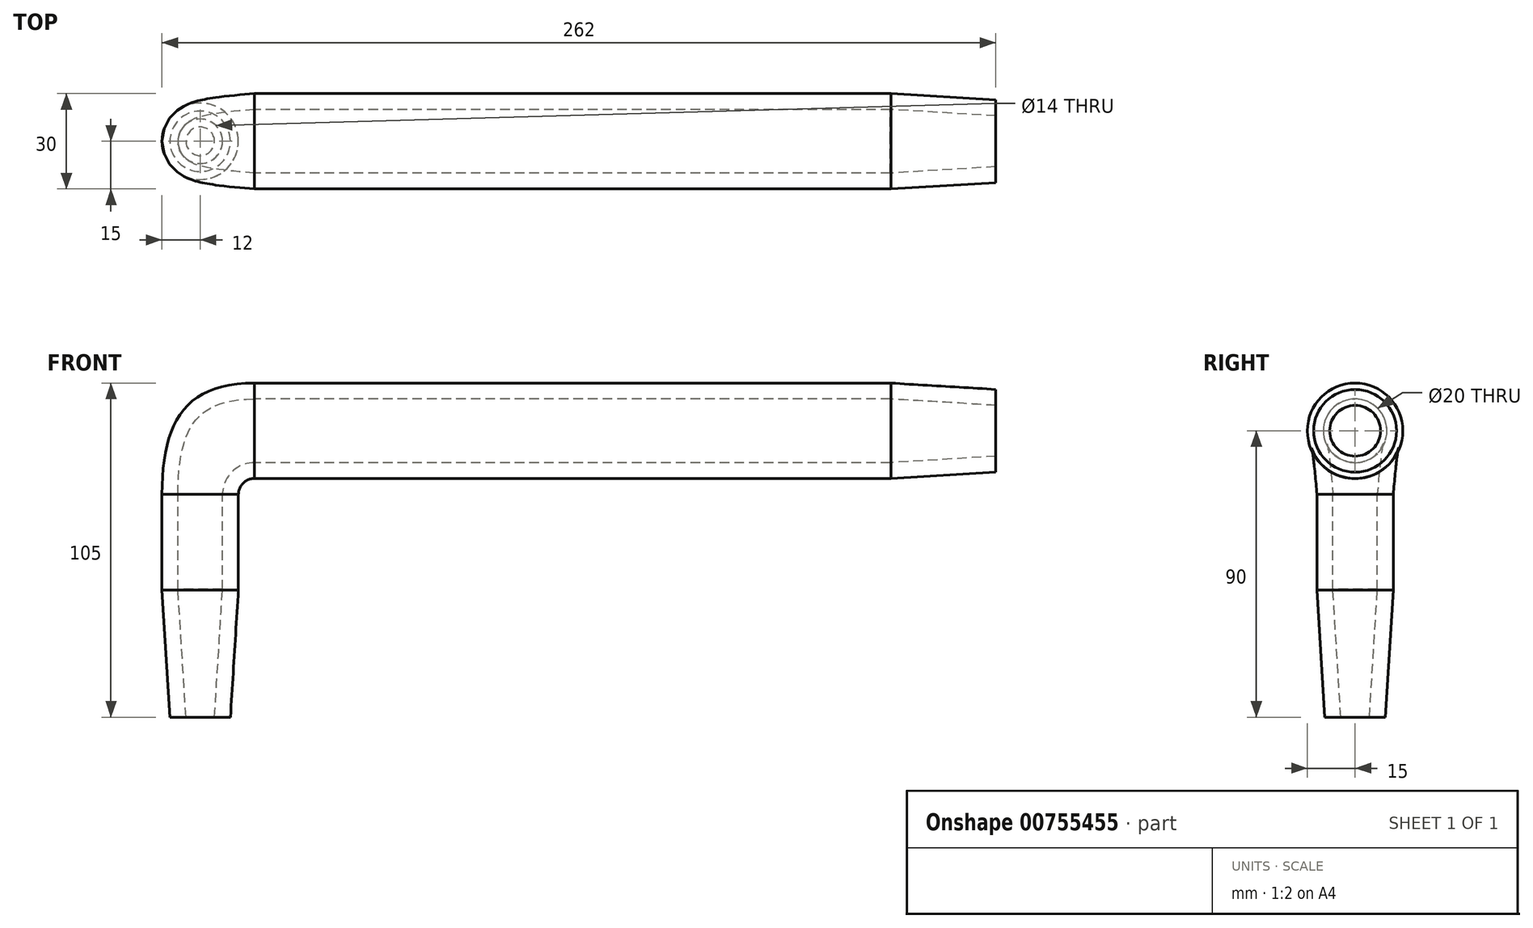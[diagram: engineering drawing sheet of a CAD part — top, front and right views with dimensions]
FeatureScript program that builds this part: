
annotation { "Feature Type Name" : "Feature", "Feature Type Description" : "" }
export const myFeature = defineFeature(function(context is Context, id is Id, definition is map)
    precondition{}
    {
        {
            var Q0;
            Q0=qCreatedBy(makeId("Front.planeOp"),FACE);
            var sketch = newSketch(context, id + "F0", { "sketchPlane" : qUnion([Q0])});
            skLineSegment(sketch, "E0", {"start": v(0, 0) * mm, "end": v(-29, 0) * mm, "construction": true});
            skLineSegment(sketch, "E1", {"start": v(0, 0) * mm, "end": v(0, 35) * mm, "construction": true});
            skArc(sketch, "E2", {"start": v(0, 5) * mm, "mid": v(-3.54, 3.54) * mm, "end": v(-5, 0) * mm});
            skFitSpline(sketch, "E3", {"points": [v(0, 35) * mm, v(-29, 0) * mm], "startDerivative": vector(-66.6, 0) * mm, "endDerivative": vector(0, -66.6) * mm});
            skLineSegment(sketch, "E4", {"start": v(0, 35) * mm, "end": v(18.57, 35) * mm, "construction": true});
            skLineSegment(sketch, "E5", {"start": v(-29, 0) * mm, "end": v(-29, -20.06) * mm, "construction": true});
            skSolve(sketch);
        }
        {
            var Q0;
            Q0=qCreatedBy(makeId("Top.planeOp"),FACE);
            var sketch = newSketch(context, id + "F1", { "sketchPlane" : qUnion([Q0])});
            skCircle(sketch, "E6", {"center": v(-17, 0) * mm, "radius": 12 * mm});
            skSolve(sketch);
        }
        {
            var Q0;
            Q0=qCreatedBy(makeId("Right.planeOp"),FACE);
            var sketch = newSketch(context, id + "F2", { "sketchPlane" : qUnion([Q0])});
            skCircle(sketch, "E7", {"center": v(0, 20) * mm, "radius": 15 * mm});
            skSolve(sketch);
        }
        {
            var Q0;
            Q0=makeQuery(id+"F1.imprint","IMPRINT",FACE,{"disambiguationData":[TD([[makeQuery(id+"F1.imprint","IMPRINT",EDGE,{"derivedFrom":sQuery(id+"F1.wireOp",EDGE,"E6")}),1.0]])]});
            var Q1;
            Q1=makeQuery(id+"F2.imprint","IMPRINT",FACE,{"disambiguationData":[TD([[makeQuery(id+"F2.imprint","IMPRINT",EDGE,{"derivedFrom":sQuery(id+"F2.wireOp",EDGE,"E7")}),1.0]])]});
            var Q2;
            Q2=sQuery(id+"F0.wireOp",EDGE,"E3");
            var Q3;
            Q3=sQuery(id+"F0.wireOp",EDGE,"E2");
            loft(context, id + "F3", {"addGuides" : true, "sheetProfilesArray" : [{ "sheetProfileEntities" : qUnion([Q0]) }, { "sheetProfileEntities" : qUnion([Q1]) }], "guidesArray" : [{ "guideEntities" : qUnion([Q2]), "guideDerivativeType" : LoftGuideDerivativeType.DEFAULT, "guideDerivativeMagnitude" : 1 }, { "guideEntities" : qUnion([Q3]), "guideDerivativeType" : LoftGuideDerivativeType.DEFAULT, "guideDerivativeMagnitude" : 1 }]});
        }
        {
            var Q0;
            Q0 = qSketchRegion(id + "F1", true);
            extrude(context, id + "F4", {"entities" : qUnion([Q0]), "operationType" : NewBodyOperationType.ADD, "oppositeDirection" : true, "depth" : 30 * mm, "offsetDistance" : 25 * mm});
        }
        {
            var Q0;
            Q0 = qSketchRegion(id + "F2", true);
            var Q1;
            Q1 = qSketchRegion(id + "F0", true);
            extrude(context, id + "F5", {"entities" : qUnion([Q0, Q1]), "operationType" : NewBodyOperationType.ADD, "depth" : 200 * mm, "offsetDistance" : 25 * mm});
        }
        {
            var Q0;
            Q0=qCreatedBy(makeId("Front.planeOp"),FACE);
            var sketch = newSketch(context, id + "F6", { "sketchPlane" : qUnion([Q0])});
            skLineSegment(sketch, "E8", {"start": v(-17, -30) * mm, "end": v(-17, -70) * mm});
            skLineSegment(sketch, "E9", {"start": v(-17, -70) * mm, "end": v(-7.5, -70) * mm});
            skLineSegment(sketch, "E10", {"start": v(-7.5, -70) * mm, "end": v(-5, -30) * mm});
            skLineSegment(sketch, "E11", {"start": v(-5, -30) * mm, "end": v(-17, -30) * mm});
            skLineSegment(sketch, "E12", {"start": v(-17, -30) * mm, "end": v(-29, -30) * mm, "construction": true});
            skSolve(sketch);
        }
        {
            var Q0;
            Q0 = qSketchRegion(id + "F6", true);
            var Q1;
            Q1=sQuery(id+"F6.wireOp",EDGE,"E8");
            revolve(context, id + "F7", {"operationType" : NewBodyOperationType.ADD, "surfaceOperationType" : NewSurfaceOperationType.NEW, "entities" : qUnion([Q0]), "axis" : qUnion([Q1]), "revolveType" : RevolveType.FULL});
        }
        {
            var Q0;
            Q0=qCreatedBy(makeId("Front.planeOp"),FACE);
            var sketch = newSketch(context, id + "F8", { "sketchPlane" : qUnion([Q0])});
            skLineSegment(sketch, "E13", {"start": v(200, 35) * mm, "end": v(200, 20) * mm});
            skLineSegment(sketch, "E14", {"start": v(200, 20) * mm, "end": v(233, 20) * mm});
            skLineSegment(sketch, "E15", {"start": v(233, 20) * mm, "end": v(233, 33) * mm});
            skLineSegment(sketch, "E16", {"start": v(233, 33) * mm, "end": v(200, 35) * mm});
            skLineSegment(sketch, "E17", {"start": v(200, 20) * mm, "end": v(200, 5) * mm, "construction": true});
            skSolve(sketch);
        }
        {
            var Q0;
            Q0 = qSketchRegion(id + "F8", true);
            var Q1;
            Q1=sQuery(id+"F8.wireOp",EDGE,"E14");
            revolve(context, id + "F9", {"operationType" : NewBodyOperationType.ADD, "surfaceOperationType" : NewSurfaceOperationType.NEW, "entities" : qUnion([Q0]), "axis" : qUnion([Q1]), "revolveType" : RevolveType.FULL});
        }
        {
            var Q0;
            Q0=makeQuery(id+"F7.opRevolve","SWEPT_FACE",FACE,{"disambiguationData":[OSD([sQuery(id+"F6.wireOp",EDGE,"E9")])]});
            var Q1;
            Q1=makeQuery(id+"F9.opRevolve","SWEPT_FACE",FACE,{"disambiguationData":[OSD([sQuery(id+"F8.wireOp",EDGE,"E15")])]});
            shell(context, id + "F10", {"entities" : qUnion([Q0, Q1]), "thickness" : 5 * mm});
        }
    });
